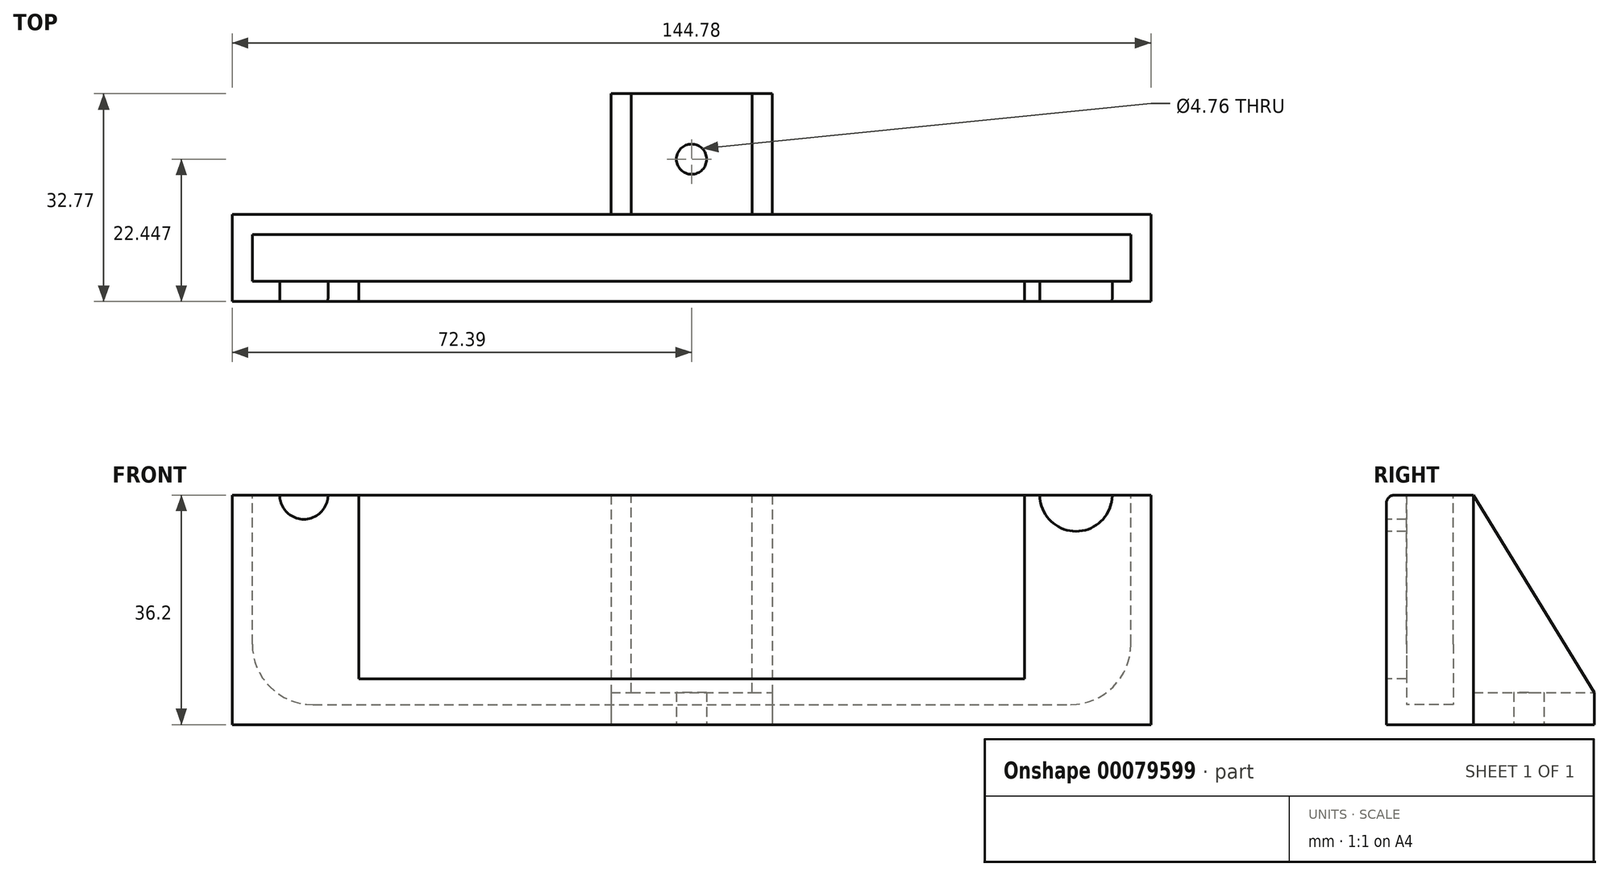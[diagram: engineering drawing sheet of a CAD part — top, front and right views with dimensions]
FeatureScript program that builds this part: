
annotation { "Feature Type Name" : "Feature", "Feature Type Description" : "" }
export const myFeature = defineFeature(function(context is Context, id is Id, definition is map)
    precondition{}
    {
        {
            var Q0;
            Q0=qCreatedBy(makeId("Top.planeOp"),FACE);
            var sketch = newSketch(context, id + "F0", { "sketchPlane" : qUnion([Q0])});
            skLineSegment(sketch, "E0.bottom", {"start": v(0, 0) * mm, "end": v(144.78, 0) * mm});
            skLineSegment(sketch, "E0.top", {"start": v(0, 13.72) * mm, "end": v(144.78, 13.72) * mm});
            skLineSegment(sketch, "E0.left", {"start": v(0, 0) * mm, "end": v(0, 13.72) * mm});
            skLineSegment(sketch, "E0.right", {"start": v(144.78, 0) * mm, "end": v(144.78, 13.72) * mm});
            skSolve(sketch);
        }
        {
            var Q0;
            Q0=makeQuery(id+"F0.imprint","IMPRINT",FACE,{"disambiguationData":[TD([[makeQuery(id+"F0.imprint","IMPRINT",EDGE,{"derivedFrom":sQuery(id+"F0.wireOp",EDGE,"E0.bottom")}),1.0]])]});
            extrude(context, id + "F1", {"entities" : qUnion([Q0]), "depth" : 36.2 * mm});
        }
        {
            var Q0;
            Q0=makeQuery(id+"F1.opExtrude","CAP_FACE",FACE,{"disambiguationData":[OSD([sQuery(id+"F0.wireOp",EDGE,"E0.bottom"),sQuery(id+"F0.wireOp",EDGE,"E0.top"),sQuery(id+"F0.wireOp",EDGE,"E0.left"),sQuery(id+"F0.wireOp",EDGE,"E0.right")])],"isStart":false});
            var sketch = newSketch(context, id + "F2", { "sketchPlane" : qUnion([Q0])});
            skLineSegment(sketch, "E1.bottom", {"start": v(3.17, 10.54) * mm, "end": v(141.6, 10.54) * mm});
            skLineSegment(sketch, "E1.top", {"start": v(3.17, 3.18) * mm, "end": v(141.6, 3.18) * mm});
            skLineSegment(sketch, "E1.left", {"start": v(3.17, 10.54) * mm, "end": v(3.18, 3.18) * mm});
            skLineSegment(sketch, "E1.right", {"start": v(141.6, 10.54) * mm, "end": v(141.6, 3.18) * mm});
            skSolve(sketch);
        }
        {
            var Q0;
            Q0=makeQuery(id+"F2.imprint","IMPRINT",FACE,{"disambiguationData":[TD([[makeQuery(id+"F2.imprint","IMPRINT",EDGE,{"derivedFrom":sQuery(id+"F2.wireOp",EDGE,"E1.bottom")}),-1.0]])]});
            extrude(context, id + "F3", {"entities" : qUnion([Q0]), "operationType" : NewBodyOperationType.REMOVE, "oppositeDirection" : true, "depth" : 33.02 * mm});
        }
        {
            var Q0;
            Q0=makeQuery(id+"F1.opExtrude","SWEPT_FACE",FACE,{"disambiguationData":[OSD([sQuery(id+"F0.wireOp",EDGE,"E0.bottom")])]});
            var sketch = newSketch(context, id + "F4", { "sketchPlane" : qUnion([Q0])});
            skLineSegment(sketch, "E2.top", {"start": v(19.94, 7.24) * mm, "end": v(124.84, 7.24) * mm});
            skLineSegment(sketch, "E2.left", {"start": v(19.94, 36.2) * mm, "end": v(19.94, 7.24) * mm});
            skLineSegment(sketch, "E2.right", {"start": v(124.84, 36.2) * mm, "end": v(124.84, 7.24) * mm});
            skCircle(sketch, "E3", {"center": v(132.97, 36.2) * mm, "radius": 5.72 * mm});
            skCircle(sketch, "E4", {"center": v(11.3, 36.2) * mm, "radius": 3.81 * mm});
            skLineSegment(sketch, "E5", {"start": v(19.94, 36.2) * mm, "end": v(15.11, 36.2) * mm});
            skLineSegment(sketch, "E6", {"start": v(7.5, 36.2) * mm, "end": v(7.5, 49.6) * mm});
            skLineSegment(sketch, "E7", {"start": v(7.5, 49.6) * mm, "end": v(141.6, 49.6) * mm});
            skLineSegment(sketch, "E8", {"start": v(141.6, 49.6) * mm, "end": v(141.6, 36.2) * mm});
            skLineSegment(sketch, "E9", {"start": v(124.84, 36.2) * mm, "end": v(127.25, 36.2) * mm});
            skSolve(sketch);
        }
        {
            var Q0;
            {var subQ0=sQuery(id+"F4.wireOp",EDGE,"E4");var subQ1=makeQuery(id+"F1.opExtrude","CAP_EDGE",EDGE,{"disambiguationData":[OSD([sQuery(id+"F0.wireOp",EDGE,"E0.bottom")])],"isStart":false});var subQ2=makeQuery(id+"F4.imprint","INTERSECT",VERTEX,{"derivedFrom":[subQ1,subQ0,sQuery(id+"F4.wireOp",EDGE,"E5")]});Q0=makeQuery(id+"F4.imprint","IMPRINT",FACE,{"disambiguationData":[TD([[makeQuery(id+"F4.imprint","IMPRINT",EDGE,{"disambiguationData":[TD([[subQ2,1.0]])],"derivedFrom":subQ0}),1.0]])]});}
            var Q1;
            Q1=makeQuery(id+"F4.imprint","IMPRINT",FACE,{"disambiguationData":[TD([[makeQuery(id+"F4.imprint","IMPRINT",EDGE,{"derivedFrom":sQuery(id+"F4.wireOp",EDGE,"E2.top")}),1.0]])]});
            var Q2;
            {var subQ0=sQuery(id+"F4.wireOp",EDGE,"E3");var subQ1=makeQuery(id+"F1.opExtrude","CAP_EDGE",EDGE,{"disambiguationData":[OSD([sQuery(id+"F0.wireOp",EDGE,"E0.bottom")])],"isStart":false});var subQ3=makeQuery(id+"F4.imprint","INTERSECT",VERTEX,{"derivedFrom":[subQ1,subQ0]});Q2=makeQuery(id+"F4.imprint","IMPRINT",FACE,{"disambiguationData":[TD([[makeQuery(id+"F4.imprint","IMPRINT",EDGE,{"disambiguationData":[TD([[subQ3,1.0]])],"derivedFrom":subQ0}),1.0]])]});}
            extrude(context, id + "F5", {"entities" : qUnion([Q0, Q1, Q2]), "operationType" : NewBodyOperationType.REMOVE, "oppositeDirection" : true, "depth" : 3.17 * mm});
        }
        {
            var Q0;
            Q0=qCreatedBy(makeId("Top.planeOp"),FACE);
            var sketch = newSketch(context, id + "F6", { "sketchPlane" : qUnion([Q0])});
            skLineSegment(sketch, "E10.bottom", {"start": v(59.7, 13.72) * mm, "end": v(85.1, 13.72) * mm});
            skLineSegment(sketch, "E10.top", {"start": v(59.7, 32.77) * mm, "end": v(85.1, 32.77) * mm});
            skLineSegment(sketch, "E10.left", {"start": v(59.7, 13.72) * mm, "end": v(59.7, 32.77) * mm});
            skLineSegment(sketch, "E10.right", {"start": v(85.1, 13.72) * mm, "end": v(85.1, 32.77) * mm});
            skSolve(sketch);
        }
        {
            var Q0;
            Q0=makeQuery(id+"F6.imprint","IMPRINT",FACE,{"disambiguationData":[TD([[makeQuery(id+"F6.imprint","IMPRINT",EDGE,{"derivedFrom":sQuery(id+"F6.wireOp",EDGE,"E10.bottom")}),1.0]])]});
            extrude(context, id + "F7", {"entities" : qUnion([Q0]), "operationType" : NewBodyOperationType.ADD, "depth" : 36.2 * mm});
        }
        {
            var Q0;
            {var subQ0=sQuery(id+"F0.wireOp",EDGE,"E0.right");var subQ1=sQuery(id+"F0.wireOp",EDGE,"E0.left");var subQ2=sQuery(id+"F0.wireOp",EDGE,"E0.top");var subQ3=sQuery(id+"F0.wireOp",EDGE,"E0.bottom");Q0=makeQuery(id+"F7.boolean.opBoolean","MERGE",FACE,{"derivedFrom":[makeQuery(id+"F5.boolean.opBoolean","SPLIT",FACE,{"disambiguationData":[TD([makeQuery(id+"F1.opExtrude","SWEPT_FACE",FACE,{"disambiguationData":[OSD([subQ2])]})])],"derivedFrom":makeQuery(id+"F1.opExtrude","CAP_FACE",FACE,{"disambiguationData":[OSD([subQ3,subQ2,subQ1,subQ0])],"isStart":false})}),makeQuery(id+"F7.opExtrude","CAP_FACE",FACE,{"disambiguationData":[OSD([sQuery(id+"F6.wireOp",EDGE,"E10.bottom"),sQuery(id+"F6.wireOp",EDGE,"E10.top"),sQuery(id+"F6.wireOp",EDGE,"E10.left"),sQuery(id+"F6.wireOp",EDGE,"E10.right")])],"isStart":false})]});}
            var sketch = newSketch(context, id + "F8", { "sketchPlane" : qUnion([Q0])});
            skLineSegment(sketch, "E11.bottom", {"start": v(81.92, 13.72) * mm, "end": v(62.87, 13.72) * mm});
            skLineSegment(sketch, "E11.top", {"start": v(81.92, 32.77) * mm, "end": v(62.87, 32.77) * mm});
            skLineSegment(sketch, "E11.left", {"start": v(81.92, 13.72) * mm, "end": v(81.92, 32.77) * mm});
            skLineSegment(sketch, "E11.right", {"start": v(62.87, 13.72) * mm, "end": v(62.87, 32.77) * mm});
            skSolve(sketch);
        }
        {
            var Q0;
            Q0=makeQuery(id+"F8.imprint","IMPRINT",FACE,{"disambiguationData":[TD([[makeQuery(id+"F8.imprint","IMPRINT",EDGE,{"derivedFrom":sQuery(id+"F8.wireOp",EDGE,"E11.bottom")}),-1.0]])]});
            extrude(context, id + "F9", {"entities" : qUnion([Q0]), "operationType" : NewBodyOperationType.REMOVE, "oppositeDirection" : true, "depth" : 31.12 * mm});
        }
        {
            var Q0;
            Q0=makeQuery(id+"F7.opExtrude","SWEPT_FACE",FACE,{"disambiguationData":[OSD([sQuery(id+"F6.wireOp",EDGE,"E10.right")])]});
            var sketch = newSketch(context, id + "F10", { "sketchPlane" : qUnion([Q0])});
            skLineSegment(sketch, "E12", {"start": v(13.72, 36.2) * mm, "end": v(32.77, 5.08) * mm});
            skLineSegment(sketch, "E13", {"start": v(32.77, 5.08) * mm, "end": v(13.72, 5.08) * mm});
            skLineSegment(sketch, "E14", {"start": v(13.72, 5.08) * mm, "end": v(13.72, 36.2) * mm});
            skSolve(sketch);
        }
        {
            var Q0;
            {var subQ0=sQuery(id+"F10.wireOp",EDGE,"E12");Q0=makeQuery(id+"F10.imprint","IMPRINT",FACE,{"disambiguationData":[TD([[makeQuery(id+"F10.imprint","IMPRINT",EDGE,{"derivedFrom":subQ0}),1.0]])]});}
            extrude(context, id + "F11", {"entities" : qUnion([Q0]), "operationType" : NewBodyOperationType.REMOVE, "oppositeDirection" : true, "depth" : 25.4 * mm});
        }
        {
            var Q0;
            Q0=makeQuery(id+"F7.boolean.opBoolean","MERGE",FACE,{"derivedFrom":[makeQuery(id+"F1.opExtrude","CAP_FACE",FACE,{"disambiguationData":[OSD([sQuery(id+"F0.wireOp",EDGE,"E0.bottom"),sQuery(id+"F0.wireOp",EDGE,"E0.top"),sQuery(id+"F0.wireOp",EDGE,"E0.left"),sQuery(id+"F0.wireOp",EDGE,"E0.right")])],"isStart":true}),makeQuery(id+"F7.opExtrude","CAP_FACE",FACE,{"disambiguationData":[OSD([sQuery(id+"F6.wireOp",EDGE,"E10.bottom"),sQuery(id+"F6.wireOp",EDGE,"E10.top"),sQuery(id+"F6.wireOp",EDGE,"E10.left"),sQuery(id+"F6.wireOp",EDGE,"E10.right")])],"isStart":true})]});
            var sketch = newSketch(context, id + "F12", { "sketchPlane" : qUnion([Q0])});
            skCircle(sketch, "E15", {"center": v(72.4, -22.45) * mm, "radius": 2.38 * mm});
            skSolve(sketch);
        }
        {
            var Q0;
            Q0=makeQuery(id+"F12.imprint","IMPRINT",FACE,{"disambiguationData":[TD([[makeQuery(id+"F12.imprint","IMPRINT",EDGE,{"derivedFrom":sQuery(id+"F12.wireOp",EDGE,"E15")}),1.0]])]});
            extrude(context, id + "F13", {"entities" : qUnion([Q0]), "operationType" : NewBodyOperationType.REMOVE, "oppositeDirection" : true, "depth" : 25.4 * mm});
        }
        {
            var Q0;
            Q0=makeQuery(id+"F3.boolean.opBoolean","COPY",EDGE,{"derivedFrom":makeQuery(id+"F3.opExtrude","CAP_EDGE",EDGE,{"disambiguationData":[OSD([sQuery(id+"F2.wireOp",EDGE,"E1.right")])],"isStart":false})});
            var Q1;
            Q1=makeQuery(id+"F3.boolean.opBoolean","COPY",EDGE,{"derivedFrom":makeQuery(id+"F3.opExtrude","CAP_EDGE",EDGE,{"disambiguationData":[OSD([sQuery(id+"F2.wireOp",EDGE,"E1.left")])],"isStart":false})});
            fillet(context, id + "F14", {"entities" : qUnion([Q0, Q1]), "radius" : 9.52 * mm, "tangentPropagation" : true, "allowEdgeOverflow" : false});
        }
        {
            var Q0;
            Q0=makeQuery(id+"F5.boolean.opBoolean","COPY",EDGE,{"derivedFrom":makeQuery(id+"F5.opExtrude","CAP_EDGE",EDGE,{"disambiguationData":[OSD([sQuery(id+"F4.wireOp",EDGE,"E2.top")])],"isStart":true})});
            var Q1;
            Q1=makeQuery(id+"F5.boolean.opBoolean","COPY",EDGE,{"derivedFrom":makeQuery(id+"F5.opExtrude","CAP_EDGE",EDGE,{"disambiguationData":[OSD([sQuery(id+"F4.wireOp",EDGE,"E3")])],"isStart":true})});
            var Q2;
            Q2=makeQuery(id+"F5.boolean.opBoolean","COPY",EDGE,{"derivedFrom":makeQuery(id+"F5.opExtrude","CAP_EDGE",EDGE,{"disambiguationData":[OSD([sQuery(id+"F4.wireOp",EDGE,"E4")])],"isStart":true})});
            var Q3;
            {var subQ0=sQuery(id+"F0.wireOp",EDGE,"E0.bottom");var subQ1=sQuery(id+"F0.wireOp",EDGE,"E0.left");Q3=makeQuery(id+"F5.boolean.opBoolean","SPLIT",EDGE,{"disambiguationData":[TD([makeQuery(id+"F1.opExtrude","SWEPT_FACE",FACE,{"disambiguationData":[OSD([subQ1])]})])],"derivedFrom":makeQuery(id+"F1.opExtrude","CAP_EDGE",EDGE,{"disambiguationData":[OSD([subQ0])],"isStart":false})});}
            var Q4;
            {var subQ0=sQuery(id+"F0.wireOp",EDGE,"E0.bottom");Q4=makeQuery(id+"F5.boolean.opBoolean","SPLIT",EDGE,{"disambiguationData":[TD([makeQuery(id+"F5.opExtrude","SWEPT_FACE",FACE,{"disambiguationData":[OSD([sQuery(id+"F4.wireOp",EDGE,"E2.left")])]})])],"derivedFrom":makeQuery(id+"F1.opExtrude","CAP_EDGE",EDGE,{"disambiguationData":[OSD([subQ0])],"isStart":false})});}
            var Q5;
            {var subQ0=sQuery(id+"F0.wireOp",EDGE,"E0.bottom");Q5=makeQuery(id+"F5.boolean.opBoolean","SPLIT",EDGE,{"disambiguationData":[TD([makeQuery(id+"F5.opExtrude","SWEPT_FACE",FACE,{"disambiguationData":[OSD([sQuery(id+"F4.wireOp",EDGE,"E2.right")])]})])],"derivedFrom":makeQuery(id+"F1.opExtrude","CAP_EDGE",EDGE,{"disambiguationData":[OSD([subQ0])],"isStart":false})});}
            var Q6;
            {var subQ0=sQuery(id+"F0.wireOp",EDGE,"E0.bottom");var subQ1=sQuery(id+"F0.wireOp",EDGE,"E0.right");Q6=makeQuery(id+"F5.boolean.opBoolean","SPLIT",EDGE,{"disambiguationData":[TD([makeQuery(id+"F1.opExtrude","SWEPT_FACE",FACE,{"disambiguationData":[OSD([subQ1])]})])],"derivedFrom":makeQuery(id+"F1.opExtrude","CAP_EDGE",EDGE,{"disambiguationData":[OSD([subQ0])],"isStart":false})});}
            var Q7;
            Q7=makeQuery(id+"F5.boolean.opBoolean","COPY",EDGE,{"derivedFrom":makeQuery(id+"F5.opExtrude","CAP_EDGE",EDGE,{"disambiguationData":[OSD([sQuery(id+"F4.wireOp",EDGE,"E2.left")])],"isStart":true})});
            var Q8;
            Q8=makeQuery(id+"F5.boolean.opBoolean","COPY",EDGE,{"derivedFrom":makeQuery(id+"F5.opExtrude","CAP_EDGE",EDGE,{"disambiguationData":[OSD([sQuery(id+"F4.wireOp",EDGE,"E2.right")])],"isStart":true})});
            fillet(context, id + "F15", {"entities" : qUnion([Q0, Q1, Q2, Q3, Q4, Q5, Q6, Q7, Q8]), "radius" : 1.27 * mm, "tangentPropagation" : true, "allowEdgeOverflow" : false});
        }
    });
